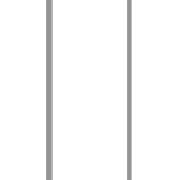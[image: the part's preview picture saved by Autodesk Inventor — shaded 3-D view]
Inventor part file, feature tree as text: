
AUTODESK INVENTOR PART (.ipt)
format: ipt  version: 2021 (Build 250183000, 183)  size: 143,360 bytes
history: native  units: in
note: dims shown in document units (in); Inventor stores cm internally (conversion verified against a paired STEP export)
features: other x4, sketch x4, plane x2, hole x1
ambient origin geometry x8: Origin, YZ Plane, XZ Plane, XY Plane, X Axis, Y Axis, Z Axis, Center Point
bodies: Solid1 (feature_tree), Body (feature_tree)
feature tree (11):
  other  "Driven Length"
  other  "Frame Generator"
  plane  "Work Plane3"
  other  "Start Plane"
  other  "End Plane"
  hole  "Hole2"  [1 undecoded]
  sketch  "Sketch"  dims[d4=2.0in d16=-0.0in d17=2.0in d18=0.12in d19=0.0in d22=1.5in d23=0.4375in d24=0.75in d25=0.635in d26=0.25in d27=0.5635in d28=1.0in d29=0.8108in d32=90.0deg d21=2.0in d8=0.5in d9=0.0344in d10=0.5in d11=0.0344in]
  sketch  "Sketch5"  dims[d0=1.5in d1=1.0in]
  sketch  "Sketch8"  dims[d2=0.0625in]
  plane  "Work Plane6"
  sketch  "Sketch9"  dims[d3=0.0625in]
note: 1 required parameter value undecoded (feature->parameter linkage not recoverable at this tier; creation-order binding heuristic only, values carry confidence <= 0.55)
